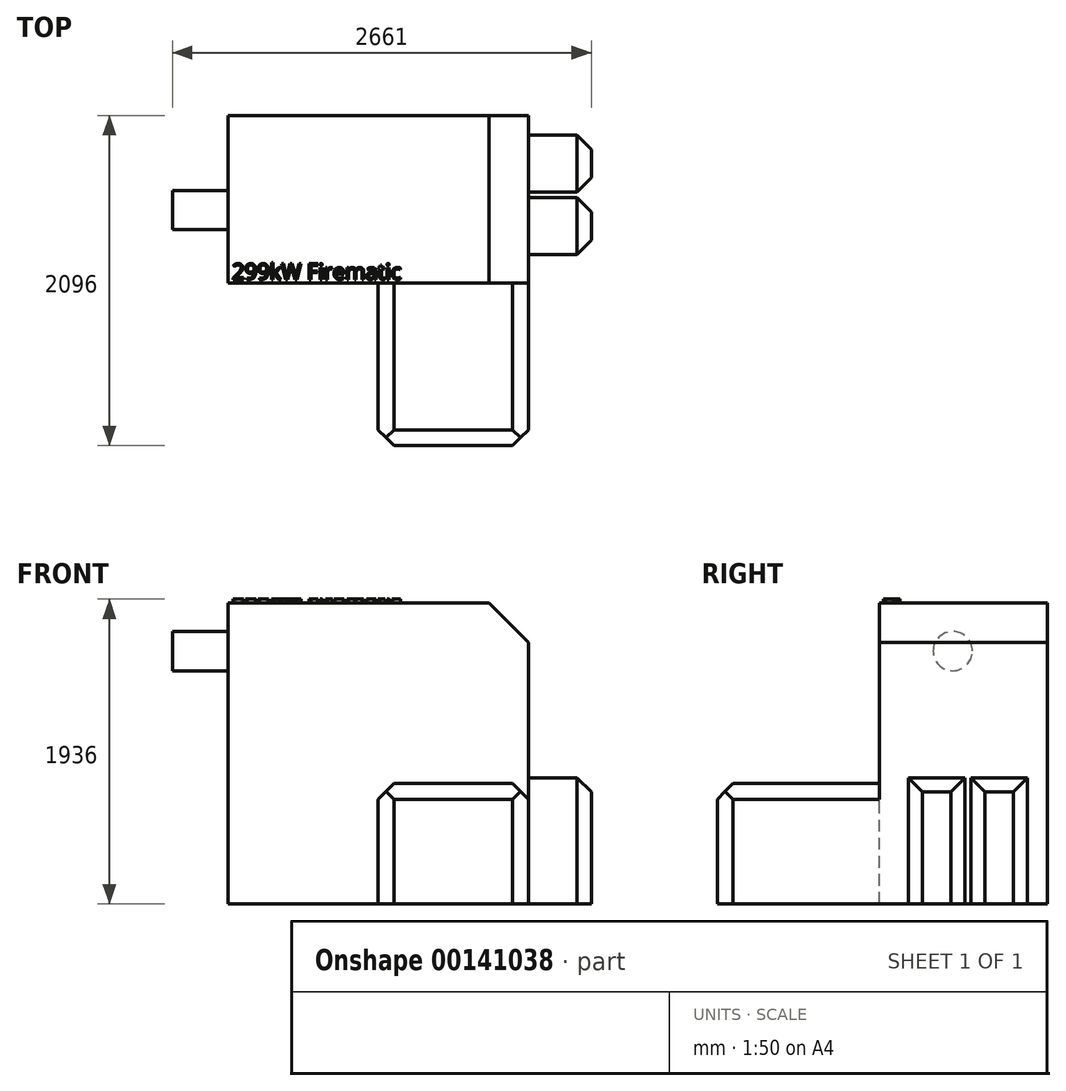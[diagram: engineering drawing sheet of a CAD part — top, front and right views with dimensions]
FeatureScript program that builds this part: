
annotation { "Feature Type Name" : "Feature", "Feature Type Description" : "" }
export const myFeature = defineFeature(function(context is Context, id is Id, definition is map)
    precondition{}
    {
        {
            var Q0;
            Q0=qCreatedBy(makeId("Top.planeOp"),FACE);
            var sketch = newSketch(context, id + "F0", { "sketchPlane" : qUnion([Q0])});
            skLineSegment(sketch, "E0.bottom", {"start": v(0, 0) * mm, "end": v(1906, 0) * mm});
            skLineSegment(sketch, "E0.top", {"start": v(0, 1065) * mm, "end": v(1906, 1065) * mm});
            skLineSegment(sketch, "E0.left", {"start": v(0, 0) * mm, "end": v(0, 1065) * mm});
            skLineSegment(sketch, "E0.right", {"start": v(1906, 0) * mm, "end": v(1906, 1065) * mm});
            skSolve(sketch);
        }
        {
            var Q0;
            Q0=qSketchRegion(id+"F0",true);
            extrude(context, id + "F1", {"entities" : qUnion([Q0]), "depth" : 1911 * mm});
        }
        {
            var Q0;
            Q0=makeQuery(id+"F1.opExtrude","CAP_FACE",FACE,{"disambiguationData":[OSD([sQuery(id+"F0.wireOp",EDGE,"E0.bottom"),sQuery(id+"F0.wireOp",EDGE,"E0.top"),sQuery(id+"F0.wireOp",EDGE,"E0.left"),sQuery(id+"F0.wireOp",EDGE,"E0.right")])],"isStart":false});
            var sketch = newSketch(context, id + "F2", { "sketchPlane" : qUnion([Q0])});
            skText(sketch, "E1", { "text": "299kW Firematic", "fontName": "OpenSans-Regular.ttf"});
            const initialGuessF2  = {"E1": [0.025, 0.025, 1, 0, 0.1]};
            skSetInitialGuess(sketch, initialGuessF2);
            skSolve(sketch);
        }
        {
            var Q0;
            Q0=qSketchRegion(id+"F2",true);
            extrude(context, id + "F3", {"entities" : qUnion([Q0]), "operationType" : NewBodyOperationType.ADD, "depth" : 25 * mm});
        }
        {
            var Q0;
            Q0=makeQuery(id+"F1.opExtrude","SWEPT_FACE",FACE,{"disambiguationData":[OSD([sQuery(id+"F0.wireOp",EDGE,"E0.bottom")])]});
            var sketch = newSketch(context, id + "F4", { "sketchPlane" : qUnion([Q0])});
            skLineSegment(sketch, "E2.bottom", {"start": v(953, 0) * mm, "end": v(1906, 0) * mm});
            skLineSegment(sketch, "E2.top", {"start": v(953, 765) * mm, "end": v(1906, 765) * mm});
            skLineSegment(sketch, "E2.left", {"start": v(953, 0) * mm, "end": v(953, 765) * mm});
            skLineSegment(sketch, "E2.right", {"start": v(1906, 0) * mm, "end": v(1906, 765) * mm});
            skSolve(sketch);
        }
        {
            var Q0;
            Q0=qSketchRegion(id+"F4",true);
            extrude(context, id + "F5", {"entities" : qUnion([Q0]), "operationType" : NewBodyOperationType.ADD, "depth" : 1031 * mm});
        }
        {
            var Q0;
            Q0=makeQuery(id+"F5.opExtrude","SWEPT_EDGE",EDGE,{"disambiguationData":[OSD([sQuery(id+"F4.wireOp",EDGE,"E2.top"),sQuery(id+"F4.wireOp",EDGE,"E2.left")])]});
            var Q1;
            Q1=makeQuery(id+"F5.opExtrude","SWEPT_EDGE",EDGE,{"disambiguationData":[OSD([sQuery(id+"F0.wireOp",EDGE,"E0.bottom"),sQuery(id+"F0.wireOp",EDGE,"E0.right"),sQuery(id+"F4.wireOp",EDGE,"E2.top"),sQuery(id+"F4.wireOp",EDGE,"E2.right")])]});
            chamfer(context, id + "F6", {"entities" : qUnion([Q0, Q1]), "width" : 100 * mm, "tangentPropagation" : true});
        }
        {
            var Q0;
            Q0=makeQuery(id+"F5.opExtrude","CAP_EDGE",EDGE,{"disambiguationData":[OSD([sQuery(id+"F4.wireOp",EDGE,"E2.top")])],"isStart":false});
            var Q1;
            Q1=makeQuery(id+"F5.opExtrude","CAP_EDGE",EDGE,{"disambiguationData":[OSD([sQuery(id+"F4.wireOp",EDGE,"E2.right")])],"isStart":false});
            var Q2;
            Q2=makeQuery(id+"F5.opExtrude","CAP_EDGE",EDGE,{"disambiguationData":[OSD([sQuery(id+"F4.wireOp",EDGE,"E2.left")])],"isStart":false});
            chamfer(context, id + "F7", {"entities" : qUnion([Q0, Q1, Q2]), "width" : 100 * mm, "tangentPropagation" : true});
        }
        {
            var Q0;
            Q0=makeQuery(id+"F1.opExtrude","SWEPT_FACE",FACE,{"disambiguationData":[OSD([sQuery(id+"F0.wireOp",EDGE,"E0.right")])]});
            var sketch = newSketch(context, id + "F8", { "sketchPlane" : qUnion([Q0])});
            skLineSegment(sketch, "E3.bottom", {"start": v(183, 0) * mm, "end": v(543, 0) * mm});
            skLineSegment(sketch, "E3.top", {"start": v(183, 800) * mm, "end": v(543, 800) * mm});
            skLineSegment(sketch, "E3.left", {"start": v(183, 0) * mm, "end": v(183, 800) * mm});
            skLineSegment(sketch, "E3.right", {"start": v(543, 0) * mm, "end": v(543, 800) * mm});
            skSolve(sketch);
        }
        {
            var Q0;
            Q0=qSketchRegion(id+"F8",true);
            extrude(context, id + "F9", {"entities" : qUnion([Q0]), "operationType" : NewBodyOperationType.ADD, "depth" : 400 * mm});
        }
        {
            var Q0;
            Q0=makeQuery(id+"F9.opExtrude","CAP_EDGE",EDGE,{"disambiguationData":[OSD([sQuery(id+"F8.wireOp",EDGE,"E3.left")])],"isStart":false});
            var Q1;
            Q1=makeQuery(id+"F9.opExtrude","CAP_EDGE",EDGE,{"disambiguationData":[OSD([sQuery(id+"F8.wireOp",EDGE,"E3.top")])],"isStart":false});
            var Q2;
            Q2=makeQuery(id+"F9.opExtrude","CAP_EDGE",EDGE,{"disambiguationData":[OSD([sQuery(id+"F8.wireOp",EDGE,"E3.right")])],"isStart":false});
            chamfer(context, id + "F10", {"entities" : qUnion([Q0, Q1, Q2]), "width" : 90 * mm, "tangentPropagation" : true});
        }
        {
            var Q0;
            Q0=makeQuery(id+"F1.opExtrude","SWEPT_FACE",FACE,{"disambiguationData":[OSD([sQuery(id+"F0.wireOp",EDGE,"E0.right")])]});
            var sketch = newSketch(context, id + "F11", { "sketchPlane" : qUnion([Q0])});
            skLineSegment(sketch, "E4.bottom", {"start": v(580, 0) * mm, "end": v(940, 0) * mm});
            skLineSegment(sketch, "E4.top", {"start": v(580, 800) * mm, "end": v(940, 800) * mm});
            skLineSegment(sketch, "E4.left", {"start": v(580, 0) * mm, "end": v(580, 800) * mm});
            skLineSegment(sketch, "E4.right", {"start": v(940, 0) * mm, "end": v(940, 800) * mm});
            skSolve(sketch);
        }
        {
            var Q0;
            Q0=qSketchRegion(id+"F11",true);
            var Q1;
            Q1=makeQuery(id+"F9.opExtrude","CAP_FACE",FACE,{"disambiguationData":[OSD([sQuery(id+"F8.wireOp",EDGE,"E3.bottom"),sQuery(id+"F8.wireOp",EDGE,"E3.top"),sQuery(id+"F8.wireOp",EDGE,"E3.left"),sQuery(id+"F8.wireOp",EDGE,"E3.right")])],"isStart":false});
            extrude(context, id + "F12", {"entities" : qUnion([Q0]), "operationType" : NewBodyOperationType.ADD, "endBound" : BoundingType.UP_TO_SURFACE, "endBoundEntityFace" : qUnion([Q1]), "depth" : 25 * mm});
        }
        {
            var Q0;
            Q0=makeQuery(id+"F12.opExtrude","CAP_EDGE",EDGE,{"disambiguationData":[OSD([sQuery(id+"F11.wireOp",EDGE,"E4.right")])],"isStart":false});
            var Q1;
            Q1=makeQuery(id+"F12.opExtrude","CAP_EDGE",EDGE,{"disambiguationData":[OSD([sQuery(id+"F11.wireOp",EDGE,"E4.top")])],"isStart":false});
            var Q2;
            Q2=makeQuery(id+"F12.opExtrude","CAP_EDGE",EDGE,{"disambiguationData":[OSD([sQuery(id+"F11.wireOp",EDGE,"E4.left")])],"isStart":false});
            chamfer(context, id + "F13", {"entities" : qUnion([Q0, Q1, Q2]), "width" : 90 * mm, "tangentPropagation" : true});
        }
        {
            var Q0;
            Q0=makeQuery(id+"F1.opExtrude","SWEPT_FACE",FACE,{"disambiguationData":[OSD([sQuery(id+"F0.wireOp",EDGE,"E0.left")])]});
            var sketch = newSketch(context, id + "F14", { "sketchPlane" : qUnion([Q0])});
            skCircle(sketch, "E5", {"center": v(-465, 1606) * mm, "radius": 125 * mm});
            skSolve(sketch);
        }
        {
            var Q0;
            Q0=qSketchRegion(id+"F14",true);
            extrude(context, id + "F15", {"entities" : qUnion([Q0]), "operationType" : NewBodyOperationType.ADD, "depth" : 355 * mm});
        }
        {
            var Q0;
            {var subQ0=sQuery(id+"F2.wireOp",EDGE,"E1.sketch_text.stroke-226");var subQ1=sQuery(id+"F0.wireOp",EDGE,"E0.top");var subQ2=sQuery(id+"F0.wireOp",EDGE,"E0.right");Q0=makeQuery(id+"F3.boolean.opBoolean","SPLIT",EDGE,{"disambiguationData":[TD([makeQuery(id+"F1.opExtrude","CAP_FACE",FACE,{"disambiguationData":[OSD([sQuery(id+"F0.wireOp",EDGE,"E0.bottom"),subQ1,sQuery(id+"F0.wireOp",EDGE,"E0.left"),subQ2])],"isStart":false}),makeQuery(id+"F1.opExtrude","SWEPT_FACE",FACE,{"disambiguationData":[OSD([subQ1])]}),makeQuery(id+"F1.opExtrude","SWEPT_FACE",FACE,{"disambiguationData":[OSD([subQ2])]}),makeQuery(id+"F3.opExtrude","CAP_FACE",FACE,{"disambiguationData":[OSD([sQuery(id+"F2.wireOp",EDGE,"E1.sketch_text.stroke-216"),sQuery(id+"F2.wireOp",EDGE,"E1.sketch_text.stroke-217"),sQuery(id+"F2.wireOp",EDGE,"E1.sketch_text.stroke-218"),sQuery(id+"F2.wireOp",EDGE,"E1.sketch_text.stroke-219"),sQuery(id+"F2.wireOp",EDGE,"E1.sketch_text.stroke-220"),sQuery(id+"F2.wireOp",EDGE,"E1.sketch_text.stroke-221"),sQuery(id+"F2.wireOp",EDGE,"E1.sketch_text.stroke-222"),sQuery(id+"F2.wireOp",EDGE,"E1.sketch_text.stroke-223"),sQuery(id+"F2.wireOp",EDGE,"E1.sketch_text.stroke-224"),sQuery(id+"F2.wireOp",EDGE,"E1.sketch_text.stroke-225"),subQ0,sQuery(id+"F2.wireOp",EDGE,"E1.sketch_text.stroke-227"),sQuery(id+"F2.wireOp",EDGE,"E1.sketch_text.stroke-228"),sQuery(id+"F2.wireOp",EDGE,"E1.sketch_text.stroke-229"),sQuery(id+"F2.wireOp",EDGE,"E1.sketch_text.stroke-230"),sQuery(id+"F2.wireOp",EDGE,"E1.sketch_text.stroke-231"),sQuery(id+"F2.wireOp",EDGE,"E1.sketch_text.stroke-232"),sQuery(id+"F2.wireOp",EDGE,"E1.sketch_text.stroke-233"),sQuery(id+"F2.wireOp",EDGE,"E1.sketch_text.stroke-234")])],"isStart":true}),makeQuery(id+"F3.opExtrude","SWEPT_FACE",FACE,{"disambiguationData":[OSD([subQ0])]})])],"derivedFrom":makeQuery(id+"F1.opExtrude","CAP_EDGE",EDGE,{"disambiguationData":[OSD([subQ2])],"isStart":false})});}
            chamfer(context, id + "F16", {"entities" : qUnion([Q0]), "width" : 250 * mm, "tangentPropagation" : true});
        }
    });
